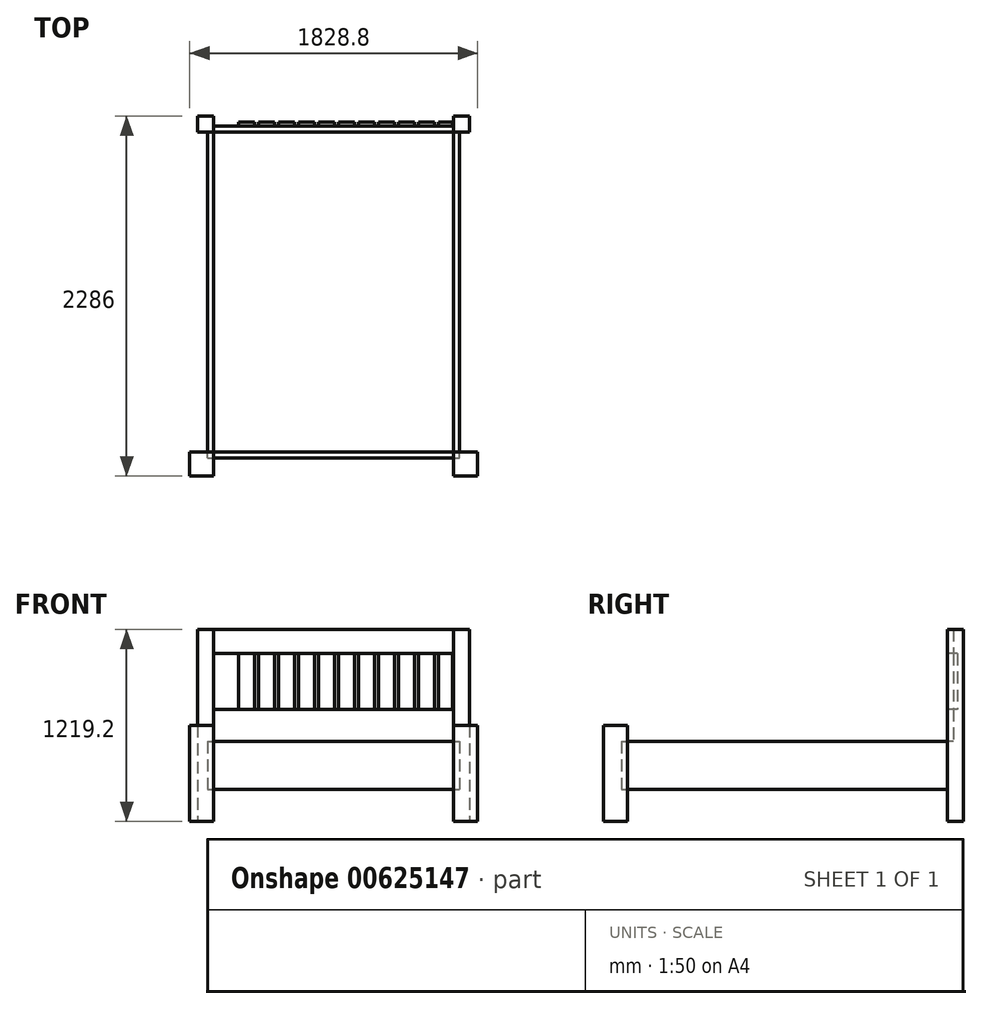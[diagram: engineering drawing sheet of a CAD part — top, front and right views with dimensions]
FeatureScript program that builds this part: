
annotation { "Feature Type Name" : "Feature", "Feature Type Description" : "" }
export const myFeature = defineFeature(function(context is Context, id is Id, definition is map)
    precondition{}
    {
        {
            var Q0;
            Q0=qCreatedBy(makeId("Top.planeOp"),FACE);
            var sketch = newSketch(context, id + "F0", { "sketchPlane" : qUnion([Q0])});
            skLineSegment(sketch, "E0.bottom", {"start": v(-863.6, 0) * mm, "end": v(-762, 0) * mm});
            skLineSegment(sketch, "E0.top", {"start": v(-863.6, 101.6) * mm, "end": v(-762, 101.6) * mm});
            skLineSegment(sketch, "E0.left", {"start": v(-863.6, 0) * mm, "end": v(-863.6, 101.6) * mm});
            skLineSegment(sketch, "E0.right", {"start": v(-762, 0) * mm, "end": v(-762, 101.6) * mm});
            skLineSegment(sketch, "E1.bottom", {"start": v(762, 0) * mm, "end": v(863.6, 0) * mm});
            skLineSegment(sketch, "E1.top", {"start": v(762, 101.6) * mm, "end": v(863.6, 101.6) * mm});
            skLineSegment(sketch, "E1.left", {"start": v(863.6, 0) * mm, "end": v(863.6, 101.6) * mm});
            skLineSegment(sketch, "E1.right", {"start": v(762, 0) * mm, "end": v(762, 101.6) * mm});
            skSolve(sketch);
        }
        {
            var Q0;
            Q0 = qSketchRegion(id + "F0", true);
            extrude(context, id + "F1", {"entities" : qUnion([Q0]), "depth" : 1219.2 * mm, "offsetDistance" : 25.4 * mm});
        }
        {
            var Q0;
            Q0=makeQuery(id+"F1.opExtrude","SWEPT_FACE",FACE,{"disambiguationData":[OSD([sQuery(id+"F0.wireOp",EDGE,"E0.bottom")])]});
            var sketch = newSketch(context, id + "F2", { "sketchPlane" : qUnion([Q0])});
            skLineSegment(sketch, "E2.bottom", {"start": v(-762, 1219.2) * mm, "end": v(762, 1219.2) * mm});
            skLineSegment(sketch, "E2.top", {"start": v(-762, 1066.8) * mm, "end": v(762, 1066.8) * mm});
            skLineSegment(sketch, "E2.left", {"start": v(-762, 1219.2) * mm, "end": v(-762, 1066.8) * mm});
            skLineSegment(sketch, "E2.right", {"start": v(762, 1219.2) * mm, "end": v(762, 1066.8) * mm});
            skLineSegment(sketch, "E3.bottom", {"start": v(-762, 711.2) * mm, "end": v(762, 711.2) * mm});
            skLineSegment(sketch, "E3.top", {"start": v(-762, 508) * mm, "end": v(762, 508) * mm});
            skLineSegment(sketch, "E3.left", {"start": v(-762, 711.2) * mm, "end": v(-762, 508) * mm});
            skLineSegment(sketch, "E3.right", {"start": v(762, 711.2) * mm, "end": v(762, 508) * mm});
            skSolve(sketch);
        }
        {
            var Q0;
            Q0 = qSketchRegion(id + "F2", true);
            extrude(context, id + "F3", {"entities" : qUnion([Q0]), "oppositeDirection" : true, "depth" : 38.1 * mm, "offsetDistance" : 25.4 * mm});
        }
        {
            var Q0;
            Q0=makeQuery(id+"F3.opExtrude","CAP_FACE",FACE,{"disambiguationData":[OSD([sQuery(id+"F2.wireOp",EDGE,"E2.bottom"),sQuery(id+"F2.wireOp",EDGE,"E2.top"),sQuery(id+"F2.wireOp",EDGE,"E2.left"),sQuery(id+"F2.wireOp",EDGE,"E2.right")])],"isStart":false});
            var sketch = newSketch(context, id + "F4", { "sketchPlane" : qUnion([Q0])});
            skLineSegment(sketch, "E4.bottom", {"start": v(-755.65, 1066.8) * mm, "end": v(-666.75, 1066.8) * mm});
            skLineSegment(sketch, "E4.top", {"start": v(-755.65, 711.2) * mm, "end": v(-666.75, 711.2) * mm});
            skLineSegment(sketch, "E4.left", {"start": v(-755.65, 1066.8) * mm, "end": v(-755.65, 711.2) * mm});
            skLineSegment(sketch, "E4.right", {"start": v(-666.75, 1066.8) * mm, "end": v(-666.75, 711.2) * mm});
            skLineSegment(sketch, "E5.bottom", {"start": v(-641.35, 1066.8) * mm, "end": v(-539.75, 1066.8) * mm});
            skLineSegment(sketch, "E5.top", {"start": v(-641.35, 711.2) * mm, "end": v(-539.75, 711.2) * mm});
            skLineSegment(sketch, "E5.left", {"start": v(-641.35, 1066.8) * mm, "end": v(-641.35, 711.2) * mm});
            skLineSegment(sketch, "E5.right", {"start": v(-539.75, 1066.8) * mm, "end": v(-539.75, 711.2) * mm});
            skLineSegment(sketch, "E6.bottom", {"start": v(-514.35, 1066.8) * mm, "end": v(-412.75, 1066.8) * mm});
            skLineSegment(sketch, "E6.top", {"start": v(-514.35, 711.2) * mm, "end": v(-412.75, 711.2) * mm});
            skLineSegment(sketch, "E6.left", {"start": v(-514.35, 1066.8) * mm, "end": v(-514.35, 711.2) * mm});
            skLineSegment(sketch, "E6.right", {"start": v(-412.75, 1066.8) * mm, "end": v(-412.75, 711.2) * mm});
            skLineSegment(sketch, "E7.bottom", {"start": v(-387.35, 1066.8) * mm, "end": v(-285.75, 1066.8) * mm});
            skLineSegment(sketch, "E7.top", {"start": v(-387.35, 711.2) * mm, "end": v(-285.75, 711.2) * mm});
            skLineSegment(sketch, "E7.left", {"start": v(-387.35, 1066.8) * mm, "end": v(-387.35, 711.2) * mm});
            skLineSegment(sketch, "E7.right", {"start": v(-285.75, 1066.8) * mm, "end": v(-285.75, 711.2) * mm});
            skLineSegment(sketch, "E8.bottom", {"start": v(-260.35, 1066.8) * mm, "end": v(-158.75, 1066.8) * mm});
            skLineSegment(sketch, "E8.top", {"start": v(-260.35, 711.2) * mm, "end": v(-158.75, 711.2) * mm});
            skLineSegment(sketch, "E8.left", {"start": v(-260.35, 1066.8) * mm, "end": v(-260.35, 711.2) * mm});
            skLineSegment(sketch, "E8.right", {"start": v(-158.75, 1066.8) * mm, "end": v(-158.75, 711.2) * mm});
            skLineSegment(sketch, "E9.bottom", {"start": v(-133.35, 1066.8) * mm, "end": v(-31.75, 1066.8) * mm});
            skLineSegment(sketch, "E9.top", {"start": v(-133.35, 711.2) * mm, "end": v(-31.75, 711.2) * mm});
            skLineSegment(sketch, "E9.left", {"start": v(-133.35, 1066.8) * mm, "end": v(-133.35, 711.2) * mm});
            skLineSegment(sketch, "E9.right", {"start": v(-31.75, 1066.8) * mm, "end": v(-31.75, 711.2) * mm});
            skLineSegment(sketch, "E10.bottom", {"start": v(-6.35, 1066.8) * mm, "end": v(95.25, 1066.8) * mm});
            skLineSegment(sketch, "E10.top", {"start": v(-6.35, 711.2) * mm, "end": v(95.25, 711.2) * mm});
            skLineSegment(sketch, "E10.left", {"start": v(-6.35, 1066.8) * mm, "end": v(-6.35, 711.2) * mm});
            skLineSegment(sketch, "E10.right", {"start": v(95.25, 1066.8) * mm, "end": v(95.25, 711.2) * mm});
            skLineSegment(sketch, "E11.bottom", {"start": v(120.65, 1066.8) * mm, "end": v(222.25, 1066.8) * mm});
            skLineSegment(sketch, "E11.top", {"start": v(120.65, 711.2) * mm, "end": v(222.25, 711.2) * mm});
            skLineSegment(sketch, "E11.left", {"start": v(120.65, 1066.8) * mm, "end": v(120.65, 711.2) * mm});
            skLineSegment(sketch, "E11.right", {"start": v(222.25, 1066.8) * mm, "end": v(222.25, 711.2) * mm});
            skLineSegment(sketch, "E12.bottom", {"start": v(247.65, 1066.8) * mm, "end": v(349.25, 1066.8) * mm});
            skLineSegment(sketch, "E12.top", {"start": v(247.65, 711.2) * mm, "end": v(349.25, 711.2) * mm});
            skLineSegment(sketch, "E12.left", {"start": v(247.65, 1066.8) * mm, "end": v(247.65, 711.2) * mm});
            skLineSegment(sketch, "E12.right", {"start": v(349.25, 1066.8) * mm, "end": v(349.25, 711.2) * mm});
            skLineSegment(sketch, "E13.bottom", {"start": v(374.65, 1066.8) * mm, "end": v(476.25, 1066.8) * mm});
            skLineSegment(sketch, "E13.top", {"start": v(374.65, 711.2) * mm, "end": v(476.25, 711.2) * mm});
            skLineSegment(sketch, "E13.left", {"start": v(374.65, 1066.8) * mm, "end": v(374.65, 711.2) * mm});
            skLineSegment(sketch, "E13.right", {"start": v(476.25, 1066.8) * mm, "end": v(476.25, 711.2) * mm});
            skLineSegment(sketch, "E14.bottom", {"start": v(501.65, 1066.8) * mm, "end": v(603.25, 1066.8) * mm});
            skLineSegment(sketch, "E14.top", {"start": v(501.65, 711.2) * mm, "end": v(603.25, 711.2) * mm});
            skLineSegment(sketch, "E14.left", {"start": v(501.65, 1066.8) * mm, "end": v(501.65, 711.2) * mm});
            skLineSegment(sketch, "E14.right", {"start": v(603.25, 1066.8) * mm, "end": v(603.25, 711.2) * mm});
            skSolve(sketch);
        }
        {
            var Q0;
            Q0 = qSketchRegion(id + "F4", true);
            extrude(context, id + "F5", {"entities" : qUnion([Q0]), "depth" : 25.4 * mm, "offsetDistance" : 25.4 * mm});
        }
        {
            var Q0;
            Q0=makeQuery(id+"F1.opExtrude","SWEPT_FACE",FACE,{"disambiguationData":[OSD([sQuery(id+"F0.wireOp",EDGE,"E0.bottom")])]});
            var sketch = newSketch(context, id + "F6", { "sketchPlane" : qUnion([Q0])});
            skLineSegment(sketch, "E15.bottom", {"start": v(-762, 508) * mm, "end": v(-800.1, 508) * mm});
            skLineSegment(sketch, "E15.top", {"start": v(-762, 203.2) * mm, "end": v(-800.1, 203.2) * mm});
            skLineSegment(sketch, "E15.left", {"start": v(-762, 508) * mm, "end": v(-762, 203.2) * mm});
            skLineSegment(sketch, "E15.right", {"start": v(-800.1, 508) * mm, "end": v(-800.1, 203.2) * mm});
            skLineSegment(sketch, "E16.bottom", {"start": v(762, 508) * mm, "end": v(800.1, 508) * mm});
            skLineSegment(sketch, "E16.top", {"start": v(762, 203.2) * mm, "end": v(800.1, 203.2) * mm});
            skLineSegment(sketch, "E16.left", {"start": v(762, 508) * mm, "end": v(762, 203.2) * mm});
            skLineSegment(sketch, "E16.right", {"start": v(800.1, 508) * mm, "end": v(800.1, 203.2) * mm});
            skSolve(sketch);
        }
        {
            var Q0;
            Q0 = qSketchRegion(id + "F6", true);
            extrude(context, id + "F7", {"entities" : qUnion([Q0]), "depth" : 2032 * mm, "offsetDistance" : 25.4 * mm});
        }
        {
            var Q0;
            Q0=makeQuery(id+"F7.opExtrude","CAP_FACE",FACE,{"disambiguationData":[OSD([sQuery(id+"F6.wireOp",EDGE,"E15.bottom"),sQuery(id+"F6.wireOp",EDGE,"E15.top"),sQuery(id+"F6.wireOp",EDGE,"E15.left"),sQuery(id+"F6.wireOp",EDGE,"E15.right")])],"isStart":false});
            var sketch = newSketch(context, id + "F8", { "sketchPlane" : qUnion([Q0])});
            skLineSegment(sketch, "E17.bottom", {"start": v(-800.1, 508) * mm, "end": v(800.1, 508) * mm});
            skLineSegment(sketch, "E17.top", {"start": v(-800.1, 203.2) * mm, "end": v(800.1, 203.2) * mm});
            skLineSegment(sketch, "E17.left", {"start": v(-800.1, 508) * mm, "end": v(-800.1, 203.2) * mm});
            skLineSegment(sketch, "E17.right", {"start": v(800.1, 508) * mm, "end": v(800.1, 203.2) * mm});
            skSolve(sketch);
        }
        {
            var Q0;
            Q0 = qSketchRegion(id + "F8", true);
            extrude(context, id + "F9", {"entities" : qUnion([Q0]), "depth" : 38.1 * mm, "offsetDistance" : 25.4 * mm});
        }
        {
            var Q0;
            Q0=qCreatedBy(makeId("Top.planeOp"),FACE);
            var sketch = newSketch(context, id + "F10", { "sketchPlane" : qUnion([Q0])});
            skLineSegment(sketch, "E18.bottom", {"start": v(-914.4, -2184.4) * mm, "end": v(-762, -2184.4) * mm});
            skLineSegment(sketch, "E18.top", {"start": v(-914.4, -2032) * mm, "end": v(-762, -2032) * mm});
            skLineSegment(sketch, "E18.left", {"start": v(-914.4, -2184.4) * mm, "end": v(-914.4, -2032) * mm});
            skLineSegment(sketch, "E18.right", {"start": v(-762, -2184.4) * mm, "end": v(-762, -2032) * mm});
            skLineSegment(sketch, "E19.bottom", {"start": v(914.4, -2184.4) * mm, "end": v(762, -2184.4) * mm});
            skLineSegment(sketch, "E19.top", {"start": v(914.4, -2032) * mm, "end": v(762, -2032) * mm});
            skLineSegment(sketch, "E19.left", {"start": v(914.4, -2184.4) * mm, "end": v(914.4, -2032) * mm});
            skLineSegment(sketch, "E19.right", {"start": v(762, -2184.4) * mm, "end": v(762, -2032) * mm});
            skSolve(sketch);
        }
        {
            var Q0;
            Q0 = qSketchRegion(id + "F10", true);
            extrude(context, id + "F11", {"entities" : qUnion([Q0]), "depth" : 609.6 * mm, "offsetDistance" : 25.4 * mm});
        }
    });
